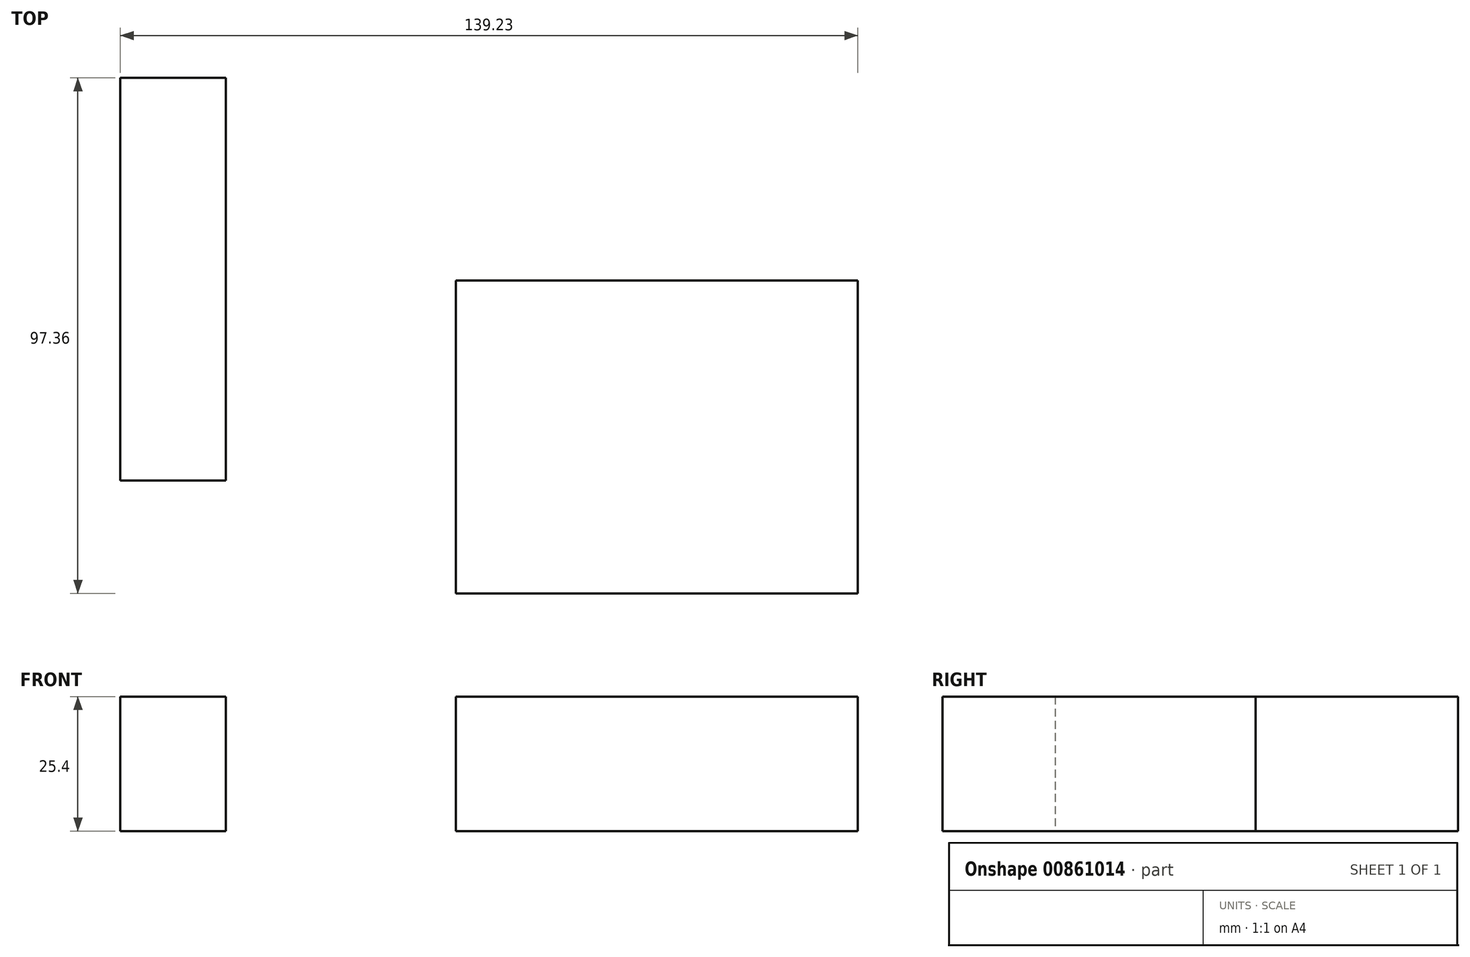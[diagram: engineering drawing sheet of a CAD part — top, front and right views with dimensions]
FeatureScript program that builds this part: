
annotation { "Feature Type Name" : "Feature", "Feature Type Description" : "" }
export const myFeature = defineFeature(function(context is Context, id is Id, definition is map)
    precondition{}
    {
        {
            var Q0;
            Q0=qCreatedBy(makeId("Top.planeOp"),FACE);
            var sketch = newSketch(context, id + "F0", { "sketchPlane" : qUnion([Q0])});
            skLineSegment(sketch, "E0.bottom", {"start": v(0, 0) * mm, "end": v(75.91, 0) * mm});
            skLineSegment(sketch, "E0.top", {"start": v(0, -59.12) * mm, "end": v(75.91, -59.12) * mm});
            skLineSegment(sketch, "E0.left", {"start": v(0, 0) * mm, "end": v(0, -59.12) * mm});
            skLineSegment(sketch, "E0.right", {"start": v(75.91, 0) * mm, "end": v(75.91, -59.12) * mm});
            skLineSegment(sketch, "E1.bottom", {"start": v(-43.38, -37.84) * mm, "end": v(-63.32, -37.84) * mm});
            skLineSegment(sketch, "E1.top", {"start": v(-43.38, 38.24) * mm, "end": v(-63.32, 38.24) * mm});
            skLineSegment(sketch, "E1.left", {"start": v(-43.38, -37.84) * mm, "end": v(-43.38, 38.24) * mm});
            skLineSegment(sketch, "E1.right", {"start": v(-63.32, -37.84) * mm, "end": v(-63.32, 38.24) * mm});
            skLineSegment(sketch, "E2.bottom", {"start": v(-103.18, -37.9) * mm, "end": v(-125.18, -37.9) * mm});
            skLineSegment(sketch, "E2.top", {"start": v(-103.18, 43.11) * mm, "end": v(-125.18, 43.11) * mm});
            skLineSegment(sketch, "E2.left", {"start": v(-103.18, -37.9) * mm, "end": v(-103.18, 43.11) * mm});
            skLineSegment(sketch, "E2.right", {"start": v(-125.18, -37.9) * mm, "end": v(-125.18, 43.11) * mm});
            skSolve(sketch);
        }
        {
            var Q0;
            Q0=makeQuery(id+"F0.imprint","IMPRINT",FACE,{"disambiguationData":[TD([[makeQuery(id+"F0.imprint","IMPRINT",EDGE,{"derivedFrom":sQuery(id+"F0.wireOp",EDGE,"E0.bottom")}),-1.0]])]});
            var Q1;
            Q1=makeQuery(id+"F0.imprint","IMPRINT",FACE,{"disambiguationData":[TD([[makeQuery(id+"F0.imprint","IMPRINT",EDGE,{"derivedFrom":sQuery(id+"F0.wireOp",EDGE,"E1.bottom")}),-1.0]])]});
            extrude(context, id + "F1", {"entities" : qUnion([Q0, Q1]), "depth" : 25.4 * mm, "offsetDistance" : 25.4 * mm});
        }
    });
